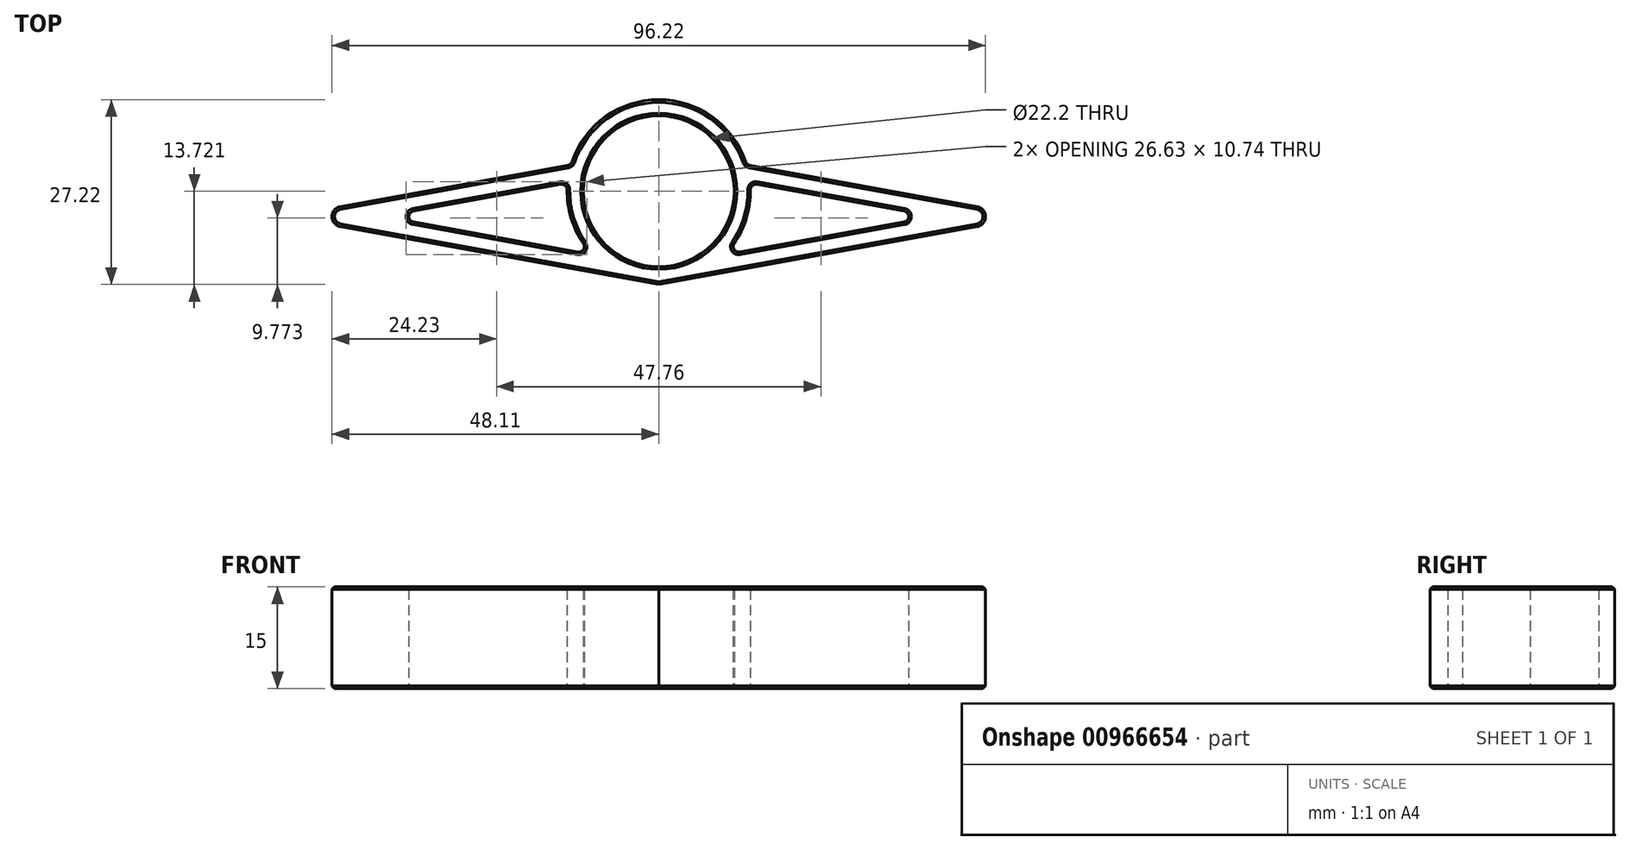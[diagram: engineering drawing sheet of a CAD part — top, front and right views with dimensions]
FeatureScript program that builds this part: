
annotation { "Feature Type Name" : "Feature", "Feature Type Description" : "" }
export const myFeature = defineFeature(function(context is Context, id is Id, definition is map)
    precondition{}
    {
        {
            var Q0;
            Q0=qCreatedBy(makeId("Top.planeOp"),FACE);
            var sketch = newSketch(context, id + "F0", { "sketchPlane" : qUnion([Q0])});
            skLineSegment(sketch, "E0", {"start": v(-55, 0) * mm, "end": v(-12.92, 7.65) * mm});
            skLineSegment(sketch, "E1", {"start": v(12.92, 7.65) * mm, "end": v(55, 0) * mm});
            skLineSegment(sketch, "E2", {"start": v(55, 0) * mm, "end": v(0, -10) * mm});
            skLineSegment(sketch, "E3", {"start": v(0, -10) * mm, "end": v(-55, 0) * mm});
            skCircle(sketch, "E4", {"center": v(0, 3.72) * mm, "radius": 13.5 * mm});
            skPoint(sketch, "E5.orphan", {"position": v(0, 10) * mm});
            skLineSegment(sketch, "E6", {"start": v(-40.47, 0) * mm, "end": v(-13.45, 4.91) * mm});
            skLineSegment(sketch, "E7", {"start": v(-40.47, 0) * mm, "end": v(-9.79, -5.58) * mm});
            skLineSegment(sketch, "E8.MirrorCS", {"start": v(40.47, 0) * mm, "end": v(9.79, -5.58) * mm});
            skLineSegment(sketch, "E9.MirrorCS", {"start": v(40.47, 0) * mm, "end": v(13.45, 4.91) * mm});
            skCircle(sketch, "E10.0", {"center": v(0, 3.72) * mm, "radius": 11.1 * mm});
            skSolve(sketch);
        }
        {
            var Q0;
            Q0 = qSketchRegion(id + "F0", true);
            extrude(context, id + "F1", {"entities" : qUnion([Q0]), "depth" : 15 * mm, "offsetDistance" : 25 * mm});
        }
        {
            var Q0;
            Q0=makeQuery(id+"F1.opExtrude","SWEPT_EDGE",EDGE,{"disambiguationData":[OSD([sQuery(id+"F0.wireOp",EDGE,"E6"),sQuery(id+"F0.wireOp",EDGE,"E7")])]});
            var Q1;
            Q1=makeQuery(id+"F1.opExtrude","SWEPT_EDGE",EDGE,{"disambiguationData":[OSD([sQuery(id+"F0.wireOp",EDGE,"E8.MirrorCS"),sQuery(id+"F0.wireOp",EDGE,"E9.MirrorCS")])]});
            var Q2;
            Q2=makeQuery(id+"F1.opExtrude","SWEPT_EDGE",EDGE,{"disambiguationData":[OSD([sQuery(id+"F0.wireOp",EDGE,"E4"),sQuery(id+"F0.wireOp",EDGE,"E7")])]});
            var Q3;
            Q3=makeQuery(id+"F1.opExtrude","SWEPT_EDGE",EDGE,{"disambiguationData":[OSD([sQuery(id+"F0.wireOp",EDGE,"E4"),sQuery(id+"F0.wireOp",EDGE,"E8.MirrorCS")])]});
            var Q4;
            Q4=makeQuery(id+"F1.opExtrude","SWEPT_EDGE",EDGE,{"disambiguationData":[OSD([sQuery(id+"F0.wireOp",EDGE,"E4"),sQuery(id+"F0.wireOp",EDGE,"E6")])]});
            var Q5;
            Q5=makeQuery(id+"F1.opExtrude","SWEPT_EDGE",EDGE,{"disambiguationData":[OSD([sQuery(id+"F0.wireOp",EDGE,"E4"),sQuery(id+"F0.wireOp",EDGE,"E9.MirrorCS")])]});
            var Q6;
            Q6=makeQuery(id+"F1.opExtrude","SWEPT_EDGE",EDGE,{"disambiguationData":[OSD([sQuery(id+"F0.wireOp",EDGE,"E1"),sQuery(id+"F0.wireOp",EDGE,"E4")])]});
            var Q7;
            Q7=makeQuery(id+"F1.opExtrude","SWEPT_EDGE",EDGE,{"disambiguationData":[OSD([sQuery(id+"F0.wireOp",EDGE,"E0"),sQuery(id+"F0.wireOp",EDGE,"E4")])]});
            fillet(context, id + "F2", {"entities" : qUnion([Q0, Q1, Q2, Q3, Q4, Q5, Q6, Q7]), "radius" : 0.8 * mm, "tangentPropagation" : true, "allowEdgeOverflow" : false});
        }
        {
            var Q0;
            Q0=makeQuery(id+"F1.opExtrude","SWEPT_EDGE",EDGE,{"disambiguationData":[OSD([sQuery(id+"F0.wireOp",EDGE,"E1"),sQuery(id+"F0.wireOp",EDGE,"E2")])]});
            var Q1;
            Q1=makeQuery(id+"F1.opExtrude","SWEPT_EDGE",EDGE,{"disambiguationData":[OSD([sQuery(id+"F0.wireOp",EDGE,"E0"),sQuery(id+"F0.wireOp",EDGE,"E3")])]});
            fillet(context, id + "F3", {"entities" : qUnion([Q0, Q1]), "radius" : 1.5 * mm, "tangentPropagation" : true, "allowEdgeOverflow" : false});
        }
        {
            var Q0;
            Q0=makeQuery(id+"F1.opExtrude","CAP_FACE",FACE,{"disambiguationData":[OSD([sQuery(id+"F0.wireOp",EDGE,"E0"),sQuery(id+"F0.wireOp",EDGE,"E1"),sQuery(id+"F0.wireOp",EDGE,"E2"),sQuery(id+"F0.wireOp",EDGE,"E3"),sQuery(id+"F0.wireOp",EDGE,"E4"),sQuery(id+"F0.wireOp",EDGE,"E6"),sQuery(id+"F0.wireOp",EDGE,"E7"),sQuery(id+"F0.wireOp",EDGE,"E8.MirrorCS"),sQuery(id+"F0.wireOp",EDGE,"E9.MirrorCS"),sQuery(id+"F0.wireOp",EDGE,"E10.0")])],"isStart":false});
            var Q1;
            Q1=makeQuery(id+"F1.opExtrude","CAP_FACE",FACE,{"disambiguationData":[OSD([sQuery(id+"F0.wireOp",EDGE,"E0"),sQuery(id+"F0.wireOp",EDGE,"E1"),sQuery(id+"F0.wireOp",EDGE,"E2"),sQuery(id+"F0.wireOp",EDGE,"E3"),sQuery(id+"F0.wireOp",EDGE,"E4"),sQuery(id+"F0.wireOp",EDGE,"E6"),sQuery(id+"F0.wireOp",EDGE,"E7"),sQuery(id+"F0.wireOp",EDGE,"E8.MirrorCS"),sQuery(id+"F0.wireOp",EDGE,"E9.MirrorCS"),sQuery(id+"F0.wireOp",EDGE,"E10.0")])],"isStart":true});
            chamfer(context, id + "F4", {"entities" : qUnion([Q0, Q1]), "width" : 0.4 * mm, "tangentPropagation" : true});
        }
    });
